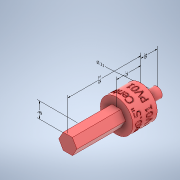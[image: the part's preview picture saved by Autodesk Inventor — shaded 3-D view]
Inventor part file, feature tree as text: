
AUTODESK INVENTOR PART (.ipt)
format: ipt  version: 2022.2 (Build 262287000, 287)  size: 1,368,576 bytes
history: native  units: in
note: dims shown in document units (in); Inventor stores cm internally (conversion verified against a paired STEP export)
features: other x7, sketch x4, extrude x3, plane x1, emboss x1
ambient origin geometry x8: Origin, YZ Plane, XZ Plane, XY Plane, X Axis, Y Axis, Z Axis, Center Point
bodies: Solid1 (feature_tree)
feature tree (16):
  other  "Annotations"
  extrude  "Hex Portion"  Depth=0.5in TaperAngle=0.0deg
  extrude  "Extrusion2"  Depth=0.75in TaperAngle=0.0deg
  other  "Reduce Size of Hex Shaft"
  extrude  "Extrusion3"  Depth=0.315in
  plane  "Work Plane1"
  emboss  "Emboss1"
  sketch  "Sketch1"  dims[d0=0.5in d1=1.5in d2=0.0in]
  sketch  "Sketch2"  dims[d3=1.0in d4=0.75in d5=0.0in]
  sketch  "Sketch3"  dims[d6=0.0075in d7=0.005in d14=0.315in]
  sketch  "Sketch4"  dims[d16=0.5in d17=0.0in d21=0.1in d22=0.0in d10=2.25in d11=0.2621in d12=0.2706in d13=0.485in d15=0.75in d18=0.5in d19=2.4445in d20=0.315in]
  other  "Linear Dimension 1"
  other  "Linear Dimension 2"
  other  "Linear Dimension 3"
  other  "Linear Dimension 4"
  other  "Diameter Dimension 1"
